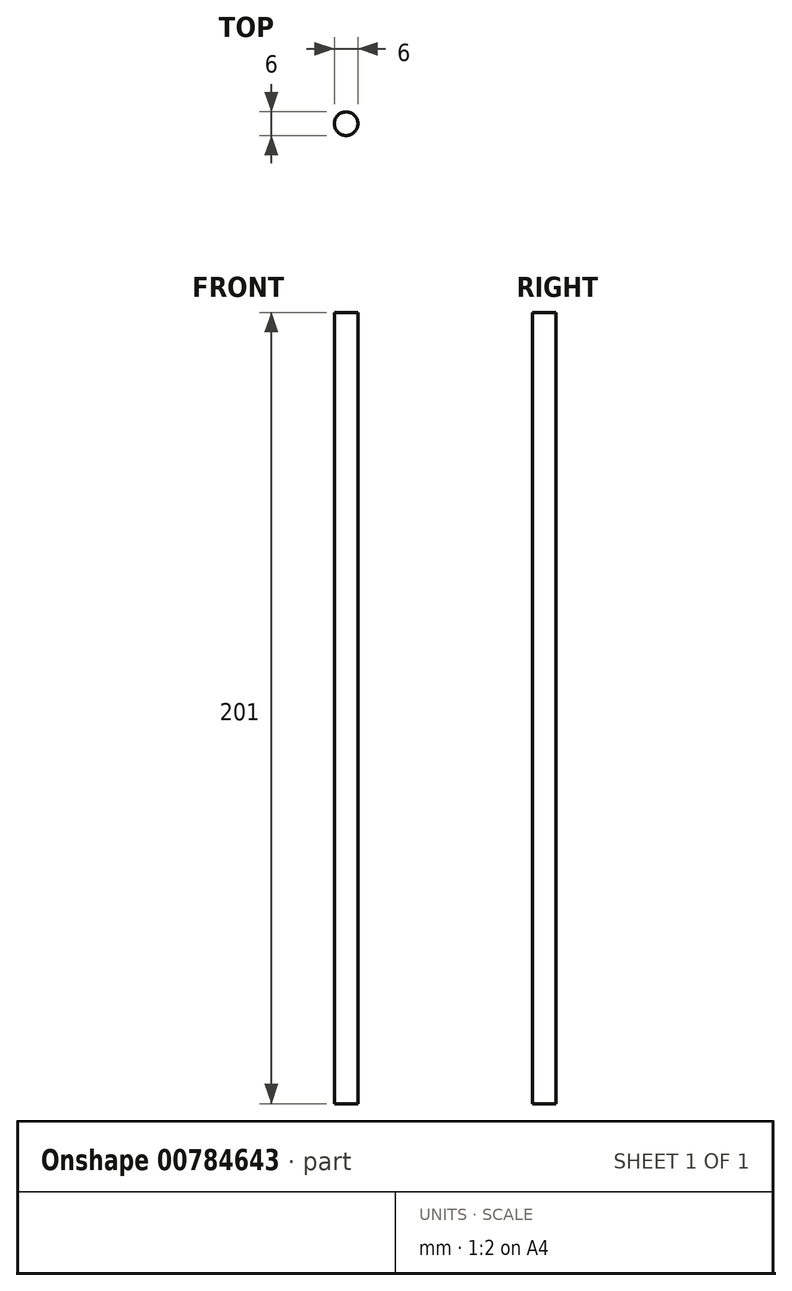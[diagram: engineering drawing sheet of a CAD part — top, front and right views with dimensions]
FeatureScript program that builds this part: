
annotation { "Feature Type Name" : "Feature", "Feature Type Description" : "" }
export const myFeature = defineFeature(function(context is Context, id is Id, definition is map)
    precondition{}
    {
        {
            var Q0;
            Q0=qCreatedBy(makeId("Top.planeOp"),FACE);
            var sketch = newSketch(context, id + "F0", { "sketchPlane" : qUnion([Q0])});
            skCircle(sketch, "E0", {"center": v(0, 0) * mm, "radius": 3 * mm});
            skSolve(sketch);
        }
        {
            var Q0;
            Q0 = qSketchRegion(id + "F0", true);
            extrude(context, id + "F1", {"entities" : qUnion([Q0]), "depth" : 201 * mm, "offsetDistance" : 25 * mm});
        }
    });
